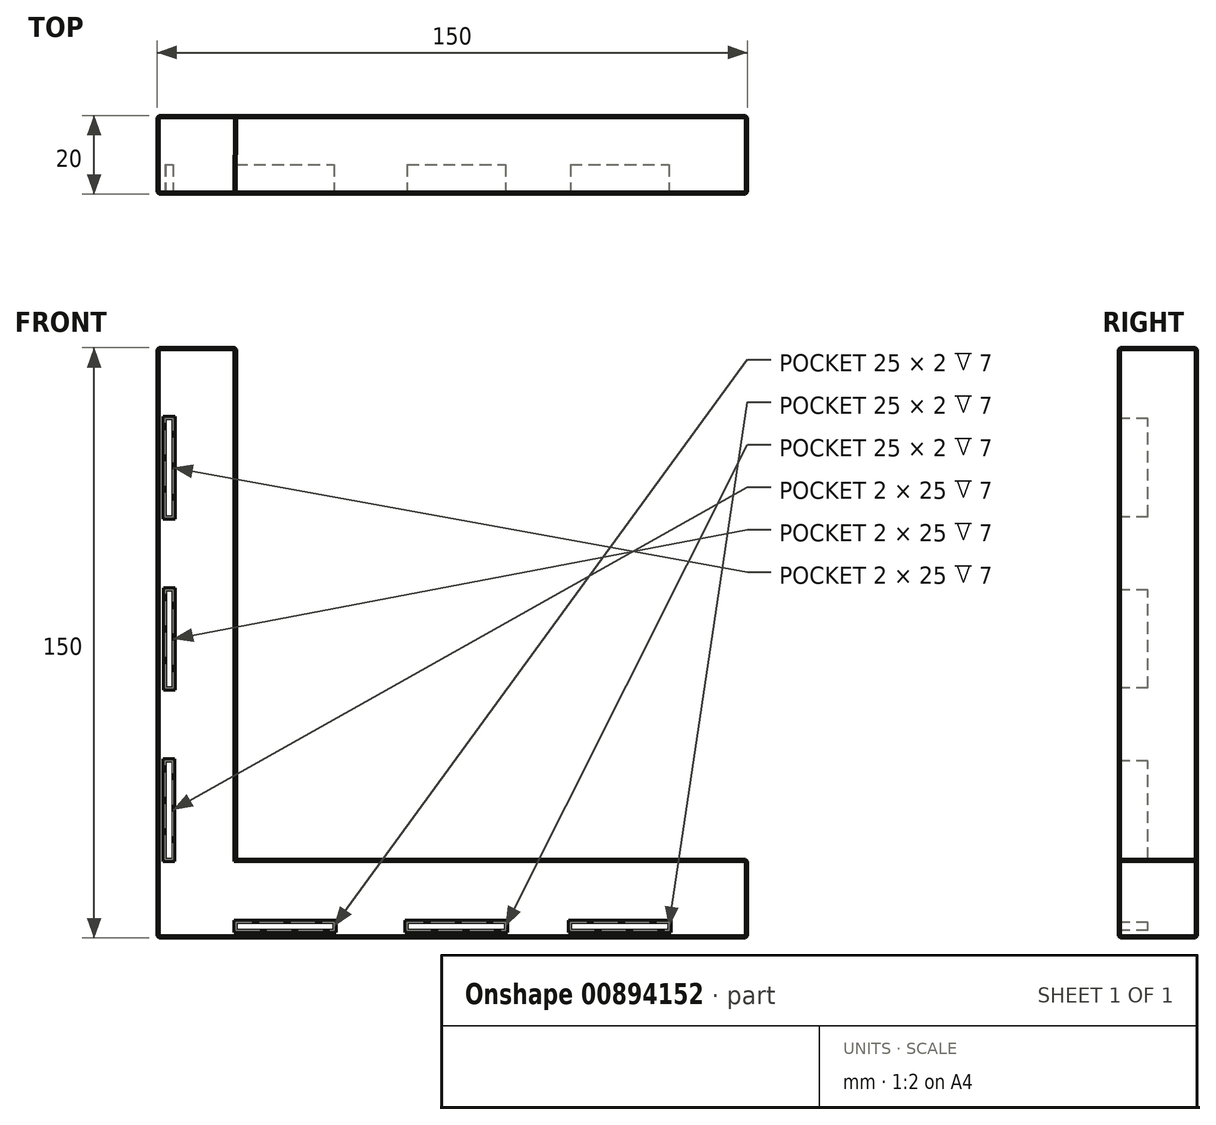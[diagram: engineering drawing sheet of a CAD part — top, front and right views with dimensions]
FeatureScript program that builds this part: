
annotation { "Feature Type Name" : "Feature", "Feature Type Description" : "" }
export const myFeature = defineFeature(function(context is Context, id is Id, definition is map)
    precondition{}
    {
        {
            var Q0;
            Q0=qCreatedBy(makeId("Top.planeOp"),FACE);
            var sketch = newSketch(context, id + "F0", { "sketchPlane" : qUnion([Q0])});
            skLineSegment(sketch, "E0.bottom", {"start": v(-63.3, 0) * mm, "end": v(-83.3, 0) * mm});
            skLineSegment(sketch, "E0.top", {"start": v(-63.07, 20) * mm, "end": v(-83.3, 20) * mm});
            skLineSegment(sketch, "E0.right", {"start": v(-83.3, 0) * mm, "end": v(-83.3, 20) * mm});
            skLineSegment(sketch, "E1.bottom", {"start": v(66.7, 0) * mm, "end": v(-83.3, 0) * mm});
            skLineSegment(sketch, "E1.top", {"start": v(66.7, 20) * mm, "end": v(-83.3, 20) * mm});
            skLineSegment(sketch, "E1.left", {"start": v(66.7, 0) * mm, "end": v(66.7, 20) * mm});
            skLineSegment(sketch, "E2", {"start": v(-63.07, 20) * mm, "end": v(-63.3, 0) * mm});
            skSolve(sketch);
        }
        {
            var Q0;
            Q0=makeQuery(id+"F0.imprint","IMPRINT",FACE,{"disambiguationData":[TD([[makeQuery(id+"F0.imprint","IMPRINT",EDGE,{"derivedFrom":sQuery(id+"F0.wireOp",EDGE,"E0.bottom")}),-1.0]])]});
            extrude(context, id + "F1", {"entities" : qUnion([Q0]), "depth" : 130 * mm, "offsetDistance" : 25 * mm});
        }
        {
            var Q0;
            Q0=makeQuery(id+"F0.imprint","IMPRINT",FACE,{"disambiguationData":[TD([[makeQuery(id+"F0.imprint","IMPRINT",EDGE,{"derivedFrom":sQuery(id+"F0.wireOp",EDGE,"E1.bottom")}),-1.0]])]});
            var Q1;
            Q1=makeQuery(id+"F0.imprint","IMPRINT",FACE,{"disambiguationData":[TD([[makeQuery(id+"F0.imprint","IMPRINT",EDGE,{"derivedFrom":sQuery(id+"F0.wireOp",EDGE,"E0.bottom")}),-1.0]])]});
            extrude(context, id + "F2", {"entities" : qUnion([Q0, Q1]), "operationType" : NewBodyOperationType.ADD, "oppositeDirection" : true, "depth" : 20 * mm, "offsetDistance" : 25 * mm});
        }
        {
            var Q0;
            Q0=qCreatedBy(makeId("Front.planeOp"),FACE);
            var sketch = newSketch(context, id + "F3", { "sketchPlane" : qUnion([Q0])});
            skLineSegment(sketch, "E3.bottom", {"start": v(-63.3, -18) * mm, "end": v(-38.3, -18) * mm});
            skLineSegment(sketch, "E3.top", {"start": v(-63.3, -16) * mm, "end": v(-38.3, -16) * mm});
            skLineSegment(sketch, "E3.left", {"start": v(-63.3, -18) * mm, "end": v(-63.3, -16) * mm});
            skLineSegment(sketch, "E3.right", {"start": v(-38.3, -18) * mm, "end": v(-38.3, -16) * mm});
            skLineSegment(sketch, "E4.bottom", {"start": v(21.7, -18) * mm, "end": v(46.7, -18) * mm});
            skLineSegment(sketch, "E4.top", {"start": v(21.7, -16) * mm, "end": v(46.7, -16) * mm});
            skLineSegment(sketch, "E4.left", {"start": v(21.7, -18) * mm, "end": v(21.7, -16) * mm});
            skLineSegment(sketch, "E4.right", {"start": v(46.7, -18) * mm, "end": v(46.7, -16) * mm});
            skLineSegment(sketch, "E5.bottom", {"start": v(-19.8, -18) * mm, "end": v(5.2, -18) * mm});
            skLineSegment(sketch, "E5.top", {"start": v(-19.8, -16) * mm, "end": v(5.2, -16) * mm});
            skLineSegment(sketch, "E5.left", {"start": v(-19.8, -18) * mm, "end": v(-19.8, -16) * mm});
            skLineSegment(sketch, "E5.right", {"start": v(5.2, -18) * mm, "end": v(5.2, -16) * mm});
            skLineSegment(sketch, "E6.bottom", {"start": v(-81.3, 0) * mm, "end": v(-79.3, 0) * mm});
            skLineSegment(sketch, "E6.top", {"start": v(-81.3, 25) * mm, "end": v(-79.3, 25) * mm});
            skLineSegment(sketch, "E6.left", {"start": v(-81.3, 0) * mm, "end": v(-81.3, 25) * mm});
            skLineSegment(sketch, "E6.right", {"start": v(-79.3, 0) * mm, "end": v(-79.3, 25) * mm});
            skLineSegment(sketch, "E7.bottom", {"start": v(-81.2, 43.5) * mm, "end": v(-79.2, 43.5) * mm});
            skLineSegment(sketch, "E7.top", {"start": v(-81.2, 68.5) * mm, "end": v(-79.2, 68.5) * mm});
            skLineSegment(sketch, "E7.left", {"start": v(-81.2, 43.5) * mm, "end": v(-81.2, 68.5) * mm});
            skLineSegment(sketch, "E7.right", {"start": v(-79.2, 43.5) * mm, "end": v(-79.2, 68.5) * mm});
            skLineSegment(sketch, "E8.bottom", {"start": v(-81.3, 87) * mm, "end": v(-79.3, 87) * mm});
            skLineSegment(sketch, "E8.top", {"start": v(-81.3, 112) * mm, "end": v(-79.3, 112) * mm});
            skLineSegment(sketch, "E8.left", {"start": v(-81.3, 87) * mm, "end": v(-81.3, 112) * mm});
            skLineSegment(sketch, "E8.right", {"start": v(-79.3, 87) * mm, "end": v(-79.3, 112) * mm});
            skSolve(sketch);
        }
        {
            var Q0;
            Q0 = qSketchRegion(id + "F3", true);
            extrude(context, id + "F4", {"entities" : qUnion([Q0]), "operationType" : NewBodyOperationType.REMOVE, "endBound" : BoundingType.SYMMETRIC, "oppositeDirection" : true, "depth" : 15 * mm, "offsetDistance" : 25 * mm});
        }
        {
            var Q0;
            {var subQ0=sQuery(id+"F0.wireOp",EDGE,"E0.bottom");Q0=makeQuery(id+"F4.boolean.opBoolean","INTERSECT",EDGE,{"derivedFrom":[makeQuery(id+"F2.boolean.opBoolean","MERGE",FACE,{"derivedFrom":[makeQuery(id+"F1.opExtrude","SWEPT_FACE",FACE,{"disambiguationData":[OSD([subQ0])]}),makeQuery(id+"F2.opExtrude","SWEPT_FACE",FACE,{"disambiguationData":[OSD([subQ0,sQuery(id+"F0.wireOp",EDGE,"E1.bottom")])]})]}),makeQuery(id+"F4.opExtrude","SWEPT_FACE",FACE,{"disambiguationData":[OSD([sQuery(id+"F3.wireOp",EDGE,"E4.top")])]})]});}
            var Q1;
            {var subQ0=sQuery(id+"F0.wireOp",EDGE,"E0.bottom");Q1=makeQuery(id+"F4.boolean.opBoolean","INTERSECT",EDGE,{"derivedFrom":[makeQuery(id+"F2.boolean.opBoolean","MERGE",FACE,{"derivedFrom":[makeQuery(id+"F1.opExtrude","SWEPT_FACE",FACE,{"disambiguationData":[OSD([subQ0])]}),makeQuery(id+"F2.opExtrude","SWEPT_FACE",FACE,{"disambiguationData":[OSD([subQ0,sQuery(id+"F0.wireOp",EDGE,"E1.bottom")])]})]}),makeQuery(id+"F4.opExtrude","SWEPT_FACE",FACE,{"disambiguationData":[OSD([sQuery(id+"F3.wireOp",EDGE,"E4.bottom")])]})]});}
            var Q2;
            {var subQ0=sQuery(id+"F0.wireOp",EDGE,"E0.bottom");Q2=makeQuery(id+"F4.boolean.opBoolean","INTERSECT",EDGE,{"derivedFrom":[makeQuery(id+"F2.boolean.opBoolean","MERGE",FACE,{"derivedFrom":[makeQuery(id+"F1.opExtrude","SWEPT_FACE",FACE,{"disambiguationData":[OSD([subQ0])]}),makeQuery(id+"F2.opExtrude","SWEPT_FACE",FACE,{"disambiguationData":[OSD([subQ0,sQuery(id+"F0.wireOp",EDGE,"E1.bottom")])]})]}),makeQuery(id+"F4.opExtrude","SWEPT_FACE",FACE,{"disambiguationData":[OSD([sQuery(id+"F3.wireOp",EDGE,"E4.right")])]})]});}
            var Q3;
            {var subQ0=sQuery(id+"F0.wireOp",EDGE,"E0.bottom");Q3=makeQuery(id+"F4.boolean.opBoolean","INTERSECT",EDGE,{"derivedFrom":[makeQuery(id+"F2.boolean.opBoolean","MERGE",FACE,{"derivedFrom":[makeQuery(id+"F1.opExtrude","SWEPT_FACE",FACE,{"disambiguationData":[OSD([subQ0])]}),makeQuery(id+"F2.opExtrude","SWEPT_FACE",FACE,{"disambiguationData":[OSD([subQ0,sQuery(id+"F0.wireOp",EDGE,"E1.bottom")])]})]}),makeQuery(id+"F4.opExtrude","SWEPT_FACE",FACE,{"disambiguationData":[OSD([sQuery(id+"F3.wireOp",EDGE,"E4.left")])]})]});}
            var Q4;
            {var subQ0=sQuery(id+"F0.wireOp",EDGE,"E0.bottom");Q4=makeQuery(id+"F4.boolean.opBoolean","INTERSECT",EDGE,{"derivedFrom":[makeQuery(id+"F2.boolean.opBoolean","MERGE",FACE,{"derivedFrom":[makeQuery(id+"F1.opExtrude","SWEPT_FACE",FACE,{"disambiguationData":[OSD([subQ0])]}),makeQuery(id+"F2.opExtrude","SWEPT_FACE",FACE,{"disambiguationData":[OSD([subQ0,sQuery(id+"F0.wireOp",EDGE,"E1.bottom")])]})]}),makeQuery(id+"F4.opExtrude","SWEPT_FACE",FACE,{"disambiguationData":[OSD([sQuery(id+"F3.wireOp",EDGE,"E5.top")])]})]});}
            var Q5;
            {var subQ0=sQuery(id+"F0.wireOp",EDGE,"E0.bottom");Q5=makeQuery(id+"F4.boolean.opBoolean","INTERSECT",EDGE,{"derivedFrom":[makeQuery(id+"F2.boolean.opBoolean","MERGE",FACE,{"derivedFrom":[makeQuery(id+"F1.opExtrude","SWEPT_FACE",FACE,{"disambiguationData":[OSD([subQ0])]}),makeQuery(id+"F2.opExtrude","SWEPT_FACE",FACE,{"disambiguationData":[OSD([subQ0,sQuery(id+"F0.wireOp",EDGE,"E1.bottom")])]})]}),makeQuery(id+"F4.opExtrude","SWEPT_FACE",FACE,{"disambiguationData":[OSD([sQuery(id+"F3.wireOp",EDGE,"E5.bottom")])]})]});}
            var Q6;
            {var subQ0=sQuery(id+"F0.wireOp",EDGE,"E0.bottom");Q6=makeQuery(id+"F4.boolean.opBoolean","INTERSECT",EDGE,{"derivedFrom":[makeQuery(id+"F2.boolean.opBoolean","MERGE",FACE,{"derivedFrom":[makeQuery(id+"F1.opExtrude","SWEPT_FACE",FACE,{"disambiguationData":[OSD([subQ0])]}),makeQuery(id+"F2.opExtrude","SWEPT_FACE",FACE,{"disambiguationData":[OSD([subQ0,sQuery(id+"F0.wireOp",EDGE,"E1.bottom")])]})]}),makeQuery(id+"F4.opExtrude","SWEPT_FACE",FACE,{"disambiguationData":[OSD([sQuery(id+"F3.wireOp",EDGE,"E5.right")])]})]});}
            var Q7;
            {var subQ0=sQuery(id+"F0.wireOp",EDGE,"E0.bottom");Q7=makeQuery(id+"F4.boolean.opBoolean","INTERSECT",EDGE,{"derivedFrom":[makeQuery(id+"F2.boolean.opBoolean","MERGE",FACE,{"derivedFrom":[makeQuery(id+"F1.opExtrude","SWEPT_FACE",FACE,{"disambiguationData":[OSD([subQ0])]}),makeQuery(id+"F2.opExtrude","SWEPT_FACE",FACE,{"disambiguationData":[OSD([subQ0,sQuery(id+"F0.wireOp",EDGE,"E1.bottom")])]})]}),makeQuery(id+"F4.opExtrude","SWEPT_FACE",FACE,{"disambiguationData":[OSD([sQuery(id+"F3.wireOp",EDGE,"E5.left")])]})]});}
            var Q8;
            {var subQ0=sQuery(id+"F0.wireOp",EDGE,"E0.bottom");Q8=makeQuery(id+"F4.boolean.opBoolean","INTERSECT",EDGE,{"derivedFrom":[makeQuery(id+"F2.boolean.opBoolean","MERGE",FACE,{"derivedFrom":[makeQuery(id+"F1.opExtrude","SWEPT_FACE",FACE,{"disambiguationData":[OSD([subQ0])]}),makeQuery(id+"F2.opExtrude","SWEPT_FACE",FACE,{"disambiguationData":[OSD([subQ0,sQuery(id+"F0.wireOp",EDGE,"E1.bottom")])]})]}),makeQuery(id+"F4.opExtrude","SWEPT_FACE",FACE,{"disambiguationData":[OSD([sQuery(id+"F3.wireOp",EDGE,"E3.right")])]})]});}
            var Q9;
            {var subQ0=sQuery(id+"F0.wireOp",EDGE,"E0.bottom");Q9=makeQuery(id+"F4.boolean.opBoolean","INTERSECT",EDGE,{"derivedFrom":[makeQuery(id+"F2.boolean.opBoolean","MERGE",FACE,{"derivedFrom":[makeQuery(id+"F1.opExtrude","SWEPT_FACE",FACE,{"disambiguationData":[OSD([subQ0])]}),makeQuery(id+"F2.opExtrude","SWEPT_FACE",FACE,{"disambiguationData":[OSD([subQ0,sQuery(id+"F0.wireOp",EDGE,"E1.bottom")])]})]}),makeQuery(id+"F4.opExtrude","SWEPT_FACE",FACE,{"disambiguationData":[OSD([sQuery(id+"F3.wireOp",EDGE,"E3.top")])]})]});}
            var Q10;
            {var subQ0=sQuery(id+"F0.wireOp",EDGE,"E0.bottom");Q10=makeQuery(id+"F4.boolean.opBoolean","INTERSECT",EDGE,{"derivedFrom":[makeQuery(id+"F2.boolean.opBoolean","MERGE",FACE,{"derivedFrom":[makeQuery(id+"F1.opExtrude","SWEPT_FACE",FACE,{"disambiguationData":[OSD([subQ0])]}),makeQuery(id+"F2.opExtrude","SWEPT_FACE",FACE,{"disambiguationData":[OSD([subQ0,sQuery(id+"F0.wireOp",EDGE,"E1.bottom")])]})]}),makeQuery(id+"F4.opExtrude","SWEPT_FACE",FACE,{"disambiguationData":[OSD([sQuery(id+"F3.wireOp",EDGE,"E3.bottom")])]})]});}
            var Q11;
            {var subQ0=sQuery(id+"F0.wireOp",EDGE,"E0.bottom");Q11=makeQuery(id+"F4.boolean.opBoolean","INTERSECT",EDGE,{"derivedFrom":[makeQuery(id+"F2.boolean.opBoolean","MERGE",FACE,{"derivedFrom":[makeQuery(id+"F1.opExtrude","SWEPT_FACE",FACE,{"disambiguationData":[OSD([subQ0])]}),makeQuery(id+"F2.opExtrude","SWEPT_FACE",FACE,{"disambiguationData":[OSD([subQ0,sQuery(id+"F0.wireOp",EDGE,"E1.bottom")])]})]}),makeQuery(id+"F4.opExtrude","SWEPT_FACE",FACE,{"disambiguationData":[OSD([sQuery(id+"F3.wireOp",EDGE,"E3.left")])]})]});}
            var Q12;
            {var subQ0=sQuery(id+"F0.wireOp",EDGE,"E0.bottom");Q12=makeQuery(id+"F4.boolean.opBoolean","INTERSECT",EDGE,{"derivedFrom":[makeQuery(id+"F2.boolean.opBoolean","MERGE",FACE,{"derivedFrom":[makeQuery(id+"F1.opExtrude","SWEPT_FACE",FACE,{"disambiguationData":[OSD([subQ0])]}),makeQuery(id+"F2.opExtrude","SWEPT_FACE",FACE,{"disambiguationData":[OSD([subQ0,sQuery(id+"F0.wireOp",EDGE,"E1.bottom")])]})]}),makeQuery(id+"F4.opExtrude","SWEPT_FACE",FACE,{"disambiguationData":[OSD([sQuery(id+"F3.wireOp",EDGE,"E6.top")])]})]});}
            var Q13;
            {var subQ0=sQuery(id+"F0.wireOp",EDGE,"E0.bottom");Q13=makeQuery(id+"F4.boolean.opBoolean","INTERSECT",EDGE,{"derivedFrom":[makeQuery(id+"F2.boolean.opBoolean","MERGE",FACE,{"derivedFrom":[makeQuery(id+"F1.opExtrude","SWEPT_FACE",FACE,{"disambiguationData":[OSD([subQ0])]}),makeQuery(id+"F2.opExtrude","SWEPT_FACE",FACE,{"disambiguationData":[OSD([subQ0,sQuery(id+"F0.wireOp",EDGE,"E1.bottom")])]})]}),makeQuery(id+"F4.opExtrude","SWEPT_FACE",FACE,{"disambiguationData":[OSD([sQuery(id+"F3.wireOp",EDGE,"E6.bottom")])]})]});}
            var Q14;
            {var subQ0=sQuery(id+"F0.wireOp",EDGE,"E0.bottom");Q14=makeQuery(id+"F4.boolean.opBoolean","INTERSECT",EDGE,{"derivedFrom":[makeQuery(id+"F2.boolean.opBoolean","MERGE",FACE,{"derivedFrom":[makeQuery(id+"F1.opExtrude","SWEPT_FACE",FACE,{"disambiguationData":[OSD([subQ0])]}),makeQuery(id+"F2.opExtrude","SWEPT_FACE",FACE,{"disambiguationData":[OSD([subQ0,sQuery(id+"F0.wireOp",EDGE,"E1.bottom")])]})]}),makeQuery(id+"F4.opExtrude","SWEPT_FACE",FACE,{"disambiguationData":[OSD([sQuery(id+"F3.wireOp",EDGE,"E6.right")])]})]});}
            var Q15;
            {var subQ0=sQuery(id+"F0.wireOp",EDGE,"E0.bottom");Q15=makeQuery(id+"F4.boolean.opBoolean","INTERSECT",EDGE,{"derivedFrom":[makeQuery(id+"F2.boolean.opBoolean","MERGE",FACE,{"derivedFrom":[makeQuery(id+"F1.opExtrude","SWEPT_FACE",FACE,{"disambiguationData":[OSD([subQ0])]}),makeQuery(id+"F2.opExtrude","SWEPT_FACE",FACE,{"disambiguationData":[OSD([subQ0,sQuery(id+"F0.wireOp",EDGE,"E1.bottom")])]})]}),makeQuery(id+"F4.opExtrude","SWEPT_FACE",FACE,{"disambiguationData":[OSD([sQuery(id+"F3.wireOp",EDGE,"E6.left")])]})]});}
            var Q16;
            {var subQ0=sQuery(id+"F0.wireOp",EDGE,"E0.bottom");Q16=makeQuery(id+"F4.boolean.opBoolean","INTERSECT",EDGE,{"derivedFrom":[makeQuery(id+"F2.boolean.opBoolean","MERGE",FACE,{"derivedFrom":[makeQuery(id+"F1.opExtrude","SWEPT_FACE",FACE,{"disambiguationData":[OSD([subQ0])]}),makeQuery(id+"F2.opExtrude","SWEPT_FACE",FACE,{"disambiguationData":[OSD([subQ0,sQuery(id+"F0.wireOp",EDGE,"E1.bottom")])]})]}),makeQuery(id+"F4.opExtrude","SWEPT_FACE",FACE,{"disambiguationData":[OSD([sQuery(id+"F3.wireOp",EDGE,"E7.bottom")])]})]});}
            var Q17;
            {var subQ0=sQuery(id+"F0.wireOp",EDGE,"E0.bottom");Q17=makeQuery(id+"F4.boolean.opBoolean","INTERSECT",EDGE,{"derivedFrom":[makeQuery(id+"F2.boolean.opBoolean","MERGE",FACE,{"derivedFrom":[makeQuery(id+"F1.opExtrude","SWEPT_FACE",FACE,{"disambiguationData":[OSD([subQ0])]}),makeQuery(id+"F2.opExtrude","SWEPT_FACE",FACE,{"disambiguationData":[OSD([subQ0,sQuery(id+"F0.wireOp",EDGE,"E1.bottom")])]})]}),makeQuery(id+"F4.opExtrude","SWEPT_FACE",FACE,{"disambiguationData":[OSD([sQuery(id+"F3.wireOp",EDGE,"E7.left")])]})]});}
            var Q18;
            {var subQ0=sQuery(id+"F0.wireOp",EDGE,"E0.bottom");Q18=makeQuery(id+"F4.boolean.opBoolean","INTERSECT",EDGE,{"derivedFrom":[makeQuery(id+"F2.boolean.opBoolean","MERGE",FACE,{"derivedFrom":[makeQuery(id+"F1.opExtrude","SWEPT_FACE",FACE,{"disambiguationData":[OSD([subQ0])]}),makeQuery(id+"F2.opExtrude","SWEPT_FACE",FACE,{"disambiguationData":[OSD([subQ0,sQuery(id+"F0.wireOp",EDGE,"E1.bottom")])]})]}),makeQuery(id+"F4.opExtrude","SWEPT_FACE",FACE,{"disambiguationData":[OSD([sQuery(id+"F3.wireOp",EDGE,"E7.right")])]})]});}
            var Q19;
            {var subQ0=sQuery(id+"F0.wireOp",EDGE,"E0.bottom");Q19=makeQuery(id+"F4.boolean.opBoolean","INTERSECT",EDGE,{"derivedFrom":[makeQuery(id+"F2.boolean.opBoolean","MERGE",FACE,{"derivedFrom":[makeQuery(id+"F1.opExtrude","SWEPT_FACE",FACE,{"disambiguationData":[OSD([subQ0])]}),makeQuery(id+"F2.opExtrude","SWEPT_FACE",FACE,{"disambiguationData":[OSD([subQ0,sQuery(id+"F0.wireOp",EDGE,"E1.bottom")])]})]}),makeQuery(id+"F4.opExtrude","SWEPT_FACE",FACE,{"disambiguationData":[OSD([sQuery(id+"F3.wireOp",EDGE,"E7.top")])]})]});}
            var Q20;
            {var subQ0=sQuery(id+"F0.wireOp",EDGE,"E0.bottom");Q20=makeQuery(id+"F4.boolean.opBoolean","INTERSECT",EDGE,{"derivedFrom":[makeQuery(id+"F2.boolean.opBoolean","MERGE",FACE,{"derivedFrom":[makeQuery(id+"F1.opExtrude","SWEPT_FACE",FACE,{"disambiguationData":[OSD([subQ0])]}),makeQuery(id+"F2.opExtrude","SWEPT_FACE",FACE,{"disambiguationData":[OSD([subQ0,sQuery(id+"F0.wireOp",EDGE,"E1.bottom")])]})]}),makeQuery(id+"F4.opExtrude","SWEPT_FACE",FACE,{"disambiguationData":[OSD([sQuery(id+"F3.wireOp",EDGE,"E8.bottom")])]})]});}
            var Q21;
            {var subQ0=sQuery(id+"F0.wireOp",EDGE,"E0.bottom");Q21=makeQuery(id+"F4.boolean.opBoolean","INTERSECT",EDGE,{"derivedFrom":[makeQuery(id+"F2.boolean.opBoolean","MERGE",FACE,{"derivedFrom":[makeQuery(id+"F1.opExtrude","SWEPT_FACE",FACE,{"disambiguationData":[OSD([subQ0])]}),makeQuery(id+"F2.opExtrude","SWEPT_FACE",FACE,{"disambiguationData":[OSD([subQ0,sQuery(id+"F0.wireOp",EDGE,"E1.bottom")])]})]}),makeQuery(id+"F4.opExtrude","SWEPT_FACE",FACE,{"disambiguationData":[OSD([sQuery(id+"F3.wireOp",EDGE,"E8.right")])]})]});}
            var Q22;
            {var subQ0=sQuery(id+"F0.wireOp",EDGE,"E0.bottom");Q22=makeQuery(id+"F4.boolean.opBoolean","INTERSECT",EDGE,{"derivedFrom":[makeQuery(id+"F2.boolean.opBoolean","MERGE",FACE,{"derivedFrom":[makeQuery(id+"F1.opExtrude","SWEPT_FACE",FACE,{"disambiguationData":[OSD([subQ0])]}),makeQuery(id+"F2.opExtrude","SWEPT_FACE",FACE,{"disambiguationData":[OSD([subQ0,sQuery(id+"F0.wireOp",EDGE,"E1.bottom")])]})]}),makeQuery(id+"F4.opExtrude","SWEPT_FACE",FACE,{"disambiguationData":[OSD([sQuery(id+"F3.wireOp",EDGE,"E8.left")])]})]});}
            var Q23;
            {var subQ0=sQuery(id+"F0.wireOp",EDGE,"E0.bottom");Q23=makeQuery(id+"F4.boolean.opBoolean","INTERSECT",EDGE,{"derivedFrom":[makeQuery(id+"F2.boolean.opBoolean","MERGE",FACE,{"derivedFrom":[makeQuery(id+"F1.opExtrude","SWEPT_FACE",FACE,{"disambiguationData":[OSD([subQ0])]}),makeQuery(id+"F2.opExtrude","SWEPT_FACE",FACE,{"disambiguationData":[OSD([subQ0,sQuery(id+"F0.wireOp",EDGE,"E1.bottom")])]})]}),makeQuery(id+"F4.opExtrude","SWEPT_FACE",FACE,{"disambiguationData":[OSD([sQuery(id+"F3.wireOp",EDGE,"E8.top")])]})]});}
            var Q24;
            {var subQ0=sQuery(id+"F0.wireOp",EDGE,"E0.right");var subQ1=sQuery(id+"F0.wireOp",EDGE,"E0.bottom");Q24=makeQuery(id+"F2.boolean.opBoolean","MERGE",EDGE,{"derivedFrom":[makeQuery(id+"F1.opExtrude","SWEPT_EDGE",EDGE,{"disambiguationData":[OSD([subQ1,subQ0])]}),makeQuery(id+"F2.opExtrude","SWEPT_EDGE",EDGE,{"disambiguationData":[OSD([subQ1,subQ0])]})]});}
            var Q25;
            Q25=makeQuery(id+"F1.opExtrude","SWEPT_EDGE",EDGE,{"disambiguationData":[OSD([sQuery(id+"F0.wireOp",EDGE,"E0.bottom"),sQuery(id+"F0.wireOp",EDGE,"E1.bottom"),sQuery(id+"F0.wireOp",EDGE,"E2")])]});
            var Q26;
            {var subQ0=sQuery(id+"F0.wireOp",EDGE,"E0.right");var subQ1=sQuery(id+"F0.wireOp",EDGE,"E0.top");Q26=makeQuery(id+"F2.boolean.opBoolean","MERGE",EDGE,{"derivedFrom":[makeQuery(id+"F1.opExtrude","SWEPT_EDGE",EDGE,{"disambiguationData":[OSD([subQ1,subQ0])]}),makeQuery(id+"F2.opExtrude","SWEPT_EDGE",EDGE,{"disambiguationData":[OSD([subQ1,subQ0])]})]});}
            var Q27;
            Q27=makeQuery(id+"F2.opExtrude","CAP_EDGE",EDGE,{"disambiguationData":[OSD([sQuery(id+"F0.wireOp",EDGE,"E0.bottom"),sQuery(id+"F0.wireOp",EDGE,"E1.bottom")])],"isStart":true});
            var Q28;
            Q28=makeQuery(id+"F2.opExtrude","CAP_EDGE",EDGE,{"disambiguationData":[OSD([sQuery(id+"F0.wireOp",EDGE,"E0.bottom"),sQuery(id+"F0.wireOp",EDGE,"E1.bottom")])],"isStart":false});
            var Q29;
            Q29=makeQuery(id+"F2.opExtrude","CAP_EDGE",EDGE,{"disambiguationData":[OSD([sQuery(id+"F0.wireOp",EDGE,"E0.top"),sQuery(id+"F0.wireOp",EDGE,"E1.top")])],"isStart":false});
            var Q30;
            Q30=makeQuery(id+"F2.opExtrude","CAP_EDGE",EDGE,{"disambiguationData":[OSD([sQuery(id+"F0.wireOp",EDGE,"E1.left")])],"isStart":true});
            var Q31;
            Q31=makeQuery(id+"F2.opExtrude","CAP_EDGE",EDGE,{"disambiguationData":[OSD([sQuery(id+"F0.wireOp",EDGE,"E1.left")])],"isStart":false});
            var Q32;
            Q32=makeQuery(id+"F2.opExtrude","CAP_EDGE",EDGE,{"disambiguationData":[OSD([sQuery(id+"F0.wireOp",EDGE,"E0.top"),sQuery(id+"F0.wireOp",EDGE,"E1.top")])],"isStart":true});
            var Q33;
            Q33=makeQuery(id+"F2.opExtrude","SWEPT_EDGE",EDGE,{"disambiguationData":[OSD([sQuery(id+"F0.wireOp",EDGE,"E1.top"),sQuery(id+"F0.wireOp",EDGE,"E1.left")])]});
            var Q34;
            Q34=makeQuery(id+"F2.opExtrude","SWEPT_EDGE",EDGE,{"disambiguationData":[OSD([sQuery(id+"F0.wireOp",EDGE,"E1.bottom"),sQuery(id+"F0.wireOp",EDGE,"E1.left")])]});
            var Q35;
            Q35=makeQuery(id+"F2.opExtrude","CAP_EDGE",EDGE,{"disambiguationData":[OSD([sQuery(id+"F0.wireOp",EDGE,"E0.right")])],"isStart":false});
            var Q36;
            Q36=makeQuery(id+"F1.opExtrude","CAP_EDGE",EDGE,{"disambiguationData":[OSD([sQuery(id+"F0.wireOp",EDGE,"E0.bottom")])],"isStart":false});
            var Q37;
            Q37=makeQuery(id+"F1.opExtrude","CAP_EDGE",EDGE,{"disambiguationData":[OSD([sQuery(id+"F0.wireOp",EDGE,"E0.right")])],"isStart":false});
            var Q38;
            Q38=makeQuery(id+"F1.opExtrude","CAP_EDGE",EDGE,{"disambiguationData":[OSD([sQuery(id+"F0.wireOp",EDGE,"E2")])],"isStart":false});
            var Q39;
            Q39=makeQuery(id+"F1.opExtrude","CAP_EDGE",EDGE,{"disambiguationData":[OSD([sQuery(id+"F0.wireOp",EDGE,"E0.top")])],"isStart":false});
            var Q40;
            Q40=makeQuery(id+"F1.opExtrude","SWEPT_EDGE",EDGE,{"disambiguationData":[OSD([sQuery(id+"F0.wireOp",EDGE,"E0.top"),sQuery(id+"F0.wireOp",EDGE,"E1.top"),sQuery(id+"F0.wireOp",EDGE,"E2")])]});
            chamfer(context, id + "F5", {"entities" : qUnion([Q0, Q1, Q2, Q3, Q4, Q5, Q6, Q7, Q8, Q9, Q10, Q11, Q12, Q13, Q14, Q15, Q16, Q17, Q18, Q19, Q20, Q21, Q22, Q23, Q24, Q25, Q26, Q27, Q28, Q29, Q30, Q31, Q32, Q33, Q34, Q35, Q36, Q37, Q38, Q39, Q40]), "width" : 0.5 * mm, "tangentPropagation" : true});
        }
    });
